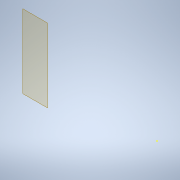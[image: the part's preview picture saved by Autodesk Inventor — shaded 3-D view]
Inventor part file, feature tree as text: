
AUTODESK INVENTOR PART (.ipt)
format: ipt  version: 2021 (Build 250183000, 183)  size: 81,920 bytes
history: native  units: mm
features: other x3, plane x1, sketch x1
ambient origin geometry x8: Origin, YZ Plane, XZ Plane, XY Plane, X Axis, Y Axis, Z Axis, Center Point
feature tree (5):
  plane  "Work Plane1"
  sketch  "Sketch1"
  other  "<userpath>\Velaverkfraedi\Vor - 2023\Tolvustud_framleidsla\lukt_samsetning.iam"
  other  "lukt_samsetning.iam"
  other  "Lukt_hlidarplata:4"
